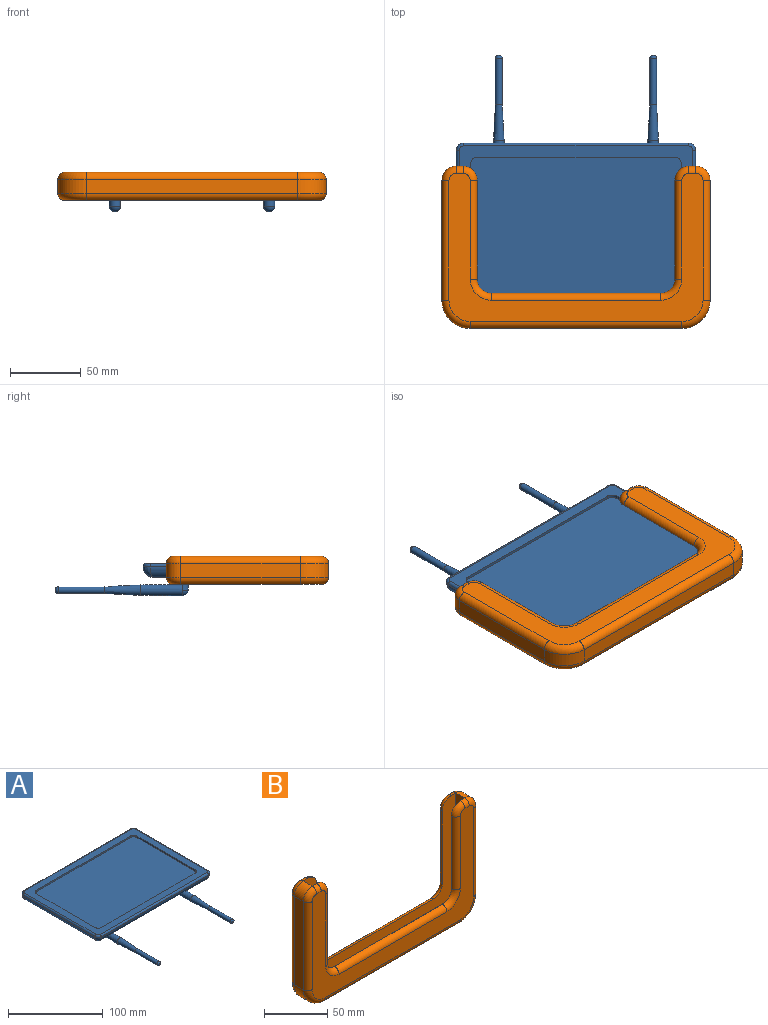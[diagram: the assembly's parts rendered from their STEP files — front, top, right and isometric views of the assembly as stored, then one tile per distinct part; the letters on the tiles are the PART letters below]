
ASSEMBLY  parts=2 mates=1
PART A: 55 faces, bbox 170.2x178.9x23 mm
  f0: plane 4x4mm, normal (0,-1,0), area 3.4mm2, adj f5,f42,f44
  f1: plane 4x4mm, normal (0,-1,0), area 3.4mm2, adj f5,f42,f44
  f2: plane 4x4mm, normal (0,-1,0), area 3.4mm2, adj f4,f41,f43
  f3: plane 4x4mm, normal (0,-1,0), area 3.4mm2, adj f4,f41,f43
  f4: plane 8x4mm, normal (0,0,-1), area 25.1mm2, adj f2,f3,f41
  f5: plane 8x4mm, normal (0,0,-1), area 25.1mm2, adj f0,f1,f42
  f6: plane 139.4x2mm, normal (0,-1,0), area 278.8mm2, adj f14,f15,f21,f24
  f7: plane 86.4x2mm, normal (-1,0,0), area 172.8mm2, adj f14,f15,f21,f22
  f8: plane 139.4x2mm, normal (0,1,0), area 278.8mm2, adj f14,f15,f22,f23
  f9: plane 106.4x0.5mm, normal (1,0,0), area 53.2mm2, adj f17,f20,f28,f36
  f10: plane 159.4x0.5mm, normal (0,1,0), area 79.7mm2, adj f17,f18,f32,f40
  f11: plane 106.4x0.5mm, normal (-1,0,0), area 53.2mm2, adj f18,f19,f29,f37
  f12: plane 159.4x0.5mm, normal (0,-1,0), area 79.7mm2, adj f19,f20,f25,f33
  f13: plane 86.4x2mm, normal (1,0,0), area 172.8mm2, adj f14,f15,f23,f24
  f14: plane 165.4x112.4mm, normal (0,0,1), area 4202.5mm2, adj f6,f7,f8,f13,f21,f22,f23,f24
  f15: plane 149.4x96.4mm, normal (0,0,1), area 14380.3mm2, adj f6,f7,f8,f13,f21,f22,f23,f24
  f16: plane 154.4x101.4mm, normal (0,0,-1), area 15555.2mm2, adj f25,f28,f29,f32,f41,f42
  f17: cylinder r=5mm len=5mm, axis (0,0,1), area 3.9mm2, adj f9,f10,f30,f38
  f18: cylinder r=5mm len=5mm, axis (0,0,-1), area 3.9mm2, adj f10,f11,f31,f39
  f19: cylinder r=5mm len=5mm, axis (0,0,1), area 3.9mm2, adj f11,f12,f27,f35
  f20: cylinder r=5mm len=5mm, axis (0,0,-1), area 3.9mm2, adj f9,f12,f26,f34
  f21: cylinder r=5mm len=5mm, axis (0,0,-1), area 15.7mm2, adj f6,f7,f14,f15
  f22: cylinder r=5mm len=5mm, axis (0,0,1), area 15.7mm2, adj f7,f8,f14,f15
  f23: cylinder r=5mm len=5mm, axis (0,0,-1), area 15.7mm2, adj f8,f13,f14,f15
  f24: cylinder r=5mm len=5mm, axis (0,0,1), area 15.7mm2, adj f6,f13,f14,f15
  f25: cylinder r=7.5mm len=159.4mm, axis (-1,0,0), area 1856.5mm2, adj f12,f16,f26,f27
  f26: bspline ~7.91x7.5mm, area 60.9mm2, adj f20,f25,f28
  f27: bspline ~7.91x7.5mm, area 60.9mm2, adj f19,f25,f29
  f28: cylinder r=7.5mm len=106.4mm, axis (0,-1,0), area 1232.1mm2, adj f9,f16,f26,f30
  f29: cylinder r=7.5mm len=106.4mm, axis (0,1,0), area 1232.1mm2, adj f11,f16,f27,f31
  f30: bspline ~7.91x7.5mm, area 60.9mm2, adj f17,f28,f32
  f31: bspline ~7.91x7.5mm, area 60.9mm2, adj f18,f29,f32
  f32: cylinder r=7.5mm len=159.4mm, axis (1,0,0), area 1856.5mm2, adj f10,f16,f30,f31
  f33: cylinder r=2mm len=159.4mm, axis (-1,0,0), area 500.8mm2, adj f12,f14,f34,f35
  f34: torus R=3mm, axis (0,0,1), area 21.1mm2, adj f14,f20,f33,f36
  f35: torus R=3mm, axis (0,0,1), area 21.1mm2, adj f14,f19,f33,f37
  f36: cylinder r=2mm len=106.4mm, axis (0,-1,0), area 334.3mm2, adj f9,f14,f34,f38
  f37: cylinder r=2mm len=106.4mm, axis (0,1,0), area 334.3mm2, adj f11,f14,f35,f39
  f38: torus R=3mm, axis (0,0,1), area 21.1mm2, adj f14,f17,f36,f40
  f39: torus R=3mm, axis (0,0,1), area 21.1mm2, adj f14,f18,f37,f40
  f40: cylinder r=2mm len=159.4mm, axis (1,0,0), area 500.8mm2, adj f10,f14,f38,f39
  f41: cylinder r=4mm len=9mm, axis (0,0,1), area 175.9mm2, adj f2,f3,f4,f16,f54
  f42: cylinder r=4mm len=9mm, axis (0,0,1), area 175.9mm2, adj f0,f1,f5,f16,f53
  f43: cone r=4mm half-angle=0.5deg, axis (0,1,0), area 729.3mm2, adj f2,f3,f45,f54
  f44: cone r=4mm half-angle=0.5deg, axis (0,1,0), area 729.3mm2, adj f0,f1,f46,f53
  f45: cone r=3.74mm half-angle=3deg, axis (0,1,0), area 485mm2, adj f43,f47
  f46: cone r=3.74mm half-angle=3deg, axis (0,1,0), area 485mm2, adj f44,f49
  f47: cylinder r=2.43mm len=33mm, axis (0,1,0), area 503.4mm2, adj f45,f52
  f48: plane 0.86x0.86mm, normal (0,-1,0), area 0.6mm2, adj f52
  f49: cylinder r=2.43mm len=33mm, axis (0,1,0), area 503.4mm2, adj f46,f51
  f50: plane 0.86x0.86mm, normal (0,-1,0), area 0.6mm2, adj f51
  f51: torus R=0.43mm, axis (0,-1,0), area 33.6mm2, adj f49,f50
  f52: torus R=0.43mm, axis (0,-1,0), area 33.6mm2, adj f47,f48
  f53: sphere r=4mm, area 50.3mm2, adj f42,f44
  f54: sphere r=4mm, area 50.3mm2, adj f41,f43
PART B: 46 faces, bbox 193.3x20x117.5 mm
  f0: plane 180x105mm, normal (0,-1,0), area 5378.5mm2, adj f28,f29,f30,f31,f32,f33,f34,f35
  f1: plane 180x105mm, normal (0,1,0), area 5378.5mm2, adj f13,f14,f15,f16,f17,f18,f19,f20
  f2: cylinder r=10mm len=10mm, axis (0,1,0), area 157.1mm2, adj f3,f11,f25,f40
  f3: plane 85x10mm, normal (-1,0,0), area 850mm2, adj f2,f27,f42,f44
  f4: plane 150x10mm, normal (0,0,-1), area 1500mm2, adj f5,f26,f41,f44
  f5: cylinder r=20mm len=20mm, axis (0,1,0), area 314.2mm2, adj f4,f6,f24,f39
  f6: plane 85x10mm, normal (1,0,0), area 850mm2, adj f5,f7,f22,f37
  f7: cylinder r=10mm len=10mm, axis (0,1,0), area 157.1mm2, adj f6,f10,f20,f35
  f8: plane 170x100mm, normal (0,-1,0), area 4400mm2, adj f10,f11,f12,f13,f14,f15,f16,f17
  f9: plane 170x100mm, normal (0,1,0), area 4400mm2, adj f10,f11,f12,f28,f29,f30,f31,f32
  f10: plane 100x10mm, normal (-1,0,0), area 1000mm2, adj f7,f8,f9,f12
  f11: plane 100x10mm, normal (1,0,0), area 1000mm2, adj f2,f8,f9,f12
  f12: plane 170x10mm, normal (0,0,1), area 1700mm2, adj f8,f9,f10,f11
  f13: torus R=15mm, axis (0,-1,0), area 145.8mm2, adj f1,f8,f14,f15
  f14: cylinder r=5mm len=70mm, axis (0,0,-1), area 549.8mm2, adj f1,f8,f13,f16
  f15: cylinder r=5mm len=120mm, axis (-1,0,0), area 942.5mm2, adj f1,f8,f13,f17
  f16: torus R=5mm, axis (0,-1,0), area 101mm2, adj f1,f8,f14,f18
  f17: torus R=15mm, axis (0,-1,0), area 145.8mm2, adj f1,f8,f15,f19
  f18: cylinder r=5mm len=5mm, axis (-1,0,0), area 39.3mm2, adj f1,f8,f16,f20
  f19: cylinder r=5mm len=70mm, axis (0,0,1), area 549.8mm2, adj f1,f8,f17,f21
  f20: torus R=5mm, axis (0,-1,0), area 101mm2, adj f1,f7,f18,f22
  f21: torus R=5mm, axis (0,-1,0), area 101mm2, adj f1,f8,f19,f23
  f22: cylinder r=5mm len=85mm, axis (0,0,1), area 667.6mm2, adj f1,f6,f20,f24
  f23: cylinder r=5mm len=5mm, axis (-1,0,0), area 39.3mm2, adj f1,f8,f21,f25
  f24: torus R=15mm, axis (0,-1,0), area 224.3mm2, adj f1,f5,f22,f26
  f25: torus R=5mm, axis (0,-1,0), area 101mm2, adj f1,f2,f23,f27
  f26: cylinder r=5mm len=150mm, axis (1,0,0), area 1178.1mm2, adj f1,f4,f24,f45
  f27: cylinder r=5mm len=85mm, axis (0,0,-1), area 667.6mm2, adj f1,f3,f25,f45
  f28: torus R=15mm, axis (0,-1,0), area 145.8mm2, adj f0,f9,f29,f30
  f29: cylinder r=5mm len=70mm, axis (0,0,1), area 549.8mm2, adj f0,f9,f28,f31
  f30: cylinder r=5mm len=120mm, axis (1,0,0), area 942.5mm2, adj f0,f9,f28,f32
  f31: torus R=5mm, axis (0,-1,0), area 101mm2, adj f0,f9,f29,f33
  f32: torus R=15mm, axis (0,-1,0), area 145.8mm2, adj f0,f9,f30,f34
  f33: cylinder r=5mm len=5mm, axis (1,0,0), area 39.3mm2, adj f0,f9,f31,f35
  f34: cylinder r=5mm len=70mm, axis (0,0,-1), area 549.8mm2, adj f0,f9,f32,f36
  f35: torus R=5mm, axis (0,-1,0), area 101mm2, adj f0,f7,f33,f37
  f36: torus R=5mm, axis (0,-1,0), area 101mm2, adj f0,f9,f34,f38
  f37: cylinder r=5mm len=85mm, axis (0,0,-1), area 667.6mm2, adj f0,f6,f35,f39
  f38: cylinder r=5mm len=5mm, axis (1,0,0), area 39.3mm2, adj f0,f9,f36,f40
  f39: torus R=15mm, axis (0,-1,0), area 224.3mm2, adj f0,f5,f37,f41
  f40: torus R=5mm, axis (0,-1,0), area 101mm2, adj f0,f2,f38,f42
  f41: cylinder r=5mm len=150mm, axis (-1,0,0), area 1178.1mm2, adj f0,f4,f39,f43
  f42: cylinder r=5mm len=85mm, axis (0,0,1), area 667.6mm2, adj f0,f3,f40,f43
  f43: torus R=15mm, axis (0,-1,0), area 224.3mm2, adj f0,f41,f42,f44
  f44: cylinder r=20mm len=20mm, axis (0,-1,0), area 314.2mm2, adj f3,f4,f43,f45
  f45: torus R=15mm, axis (0,-1,0), area 224.3mm2, adj f1,f26,f27,f44
PLACE A rot(axis=(0,0,1),180deg) t=(0,0.2,8)mm
PLACE B rot(axis=(-1,0,0),90deg) t=(0,-60.5,-5)mm
MATE fastened A.f10 <-> B.f12  axis (0,-1,0) through (0,-58,7.75)mm
